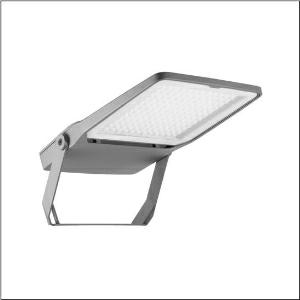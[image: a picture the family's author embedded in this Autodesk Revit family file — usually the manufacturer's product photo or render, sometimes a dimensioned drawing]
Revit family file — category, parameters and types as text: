
# Revit family: floodlight_fl_20_midi___rs17_5xa7682e3b1ac_f763
name_source: partatom
category: Lighting Fixtures
units: mm (PartAtom-declared; Revit-internal decimal feet)

## family parameters
Cut with Voids When Loaded = No
Host = Face
Light Source = No
Part Type = Normal
Room Calculation Point = No
Round Connector Dimension = Use Diameter
Shared = No

## types (1)
- --- (1 x LED 5000K / CRI = 70 (unbekannt), 29600 lm, 5000K)
    Apparent Load = 208 VA
    CIE Flux Codes = 79 92 99 100 100
    Color Rendering = 70
    Color Temperature = 5000K
    Default Elevation = 1800 mm
    Description = Floodlight FL 20 midi, floodlight, primary light control with lens, of plastic, primary optical cover: protective disc, of toughened safety glass, transparent, light distribution: RS17, light emission: direct distribution, primary light characteristic: rotationally symmetric, installation type: surface-mounted, LED, High Power LED, rated luminous flux: 29.600lm, luminous efficacy: 142lm/W, light colour: 750, colour temperature: 5000K, control gear: ECG Plus, control: flexible luminous flux parameterisation, time-dependent luminous flux control, digital communication interface, power reduction, overheat protection, electronic power reduction, with terminal, 5-pole, max. 2.5mm², mains connection: 220..240V, AC, 50/60Hz, rated input power: 208W, LED unit, of diecast aluminium, powder-coated, Siteco® metallic grey (DB 702S), corrosivity category C5 mid according to DIN EN ISO 12944, incl. 1x M20 cable gland for cable Ø 6.5..12mm, length: 654mm, width: 450mm, height: 76mm, housing frame, of diecast aluminium, powder-coated, Siteco® metallic grey (DB 702S), mounting bracket, of steel, powder-coated, Siteco® metallic grey (DB 702S), DALI, protection rating (complete): IP66, insulation class (complete): insulation class II (safety insulation), certification: CE, ENEC, VDE, protection symbol: D, permissible operating ambient temperature: -40..+40°C, permissible operating ambient temperature for outdoor applications: -40..+50°C, standard: DIN EN 12944, packaging unit: 1 piece

Light Distribution: RS17
    Height = 76 mm
    Lamp = 1 x LED 5000K / CRI >= 70 (unbekannt)
    Lamp Light Flux = 29600 lm
    Lamp count = 1
    Length = 672 mm
    Luminous efficacy = 142 lm/W
    Manufacturer = Siteco
    ModVariant = No
    Model = 5XA7682E3B1AC
    Mounting Place = Wall
    Mounting Type = Surface mounted
    Number of Poles = 1
    OnlyDefault = Yes
    Power Factor = 1
    Product Name = Floodlight FL 20 midi | RS17
    Product group = floodlight | wall mounted
    ProductGroupID = 2001
    Protection Class = Protection class II
    Protection Degree = IP 66
    RLX_Detail_Level = 1
    RLX_Emergency_Light_Flux = 0 lm
    RLX_Emergency_Type = 0
    RLX_Emergency_Type_DB = No
    RlxData = <blob elided: 92313 chars, md5=dfe36ad4>
    Socket = socket
    Standby Power = 0 W
    System Light Flux = 29600 lm
    System Power = 208 W
    Type Comments = factory setting: luminous flux: 100 % | dim-lin: 254 | 484 mA
    Type Image = l_1005943.jpg
    URL = http://relux.com
    VarID = @adj_146377
    Voltage = 0 V
    Weight = 0.00 kg
    Width = 450 mm

## geometry (parser evidence)
native form markers: Blend x4, Sweep x12
no freeform markers — native parametric forms only
